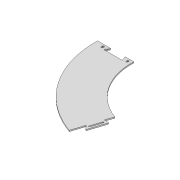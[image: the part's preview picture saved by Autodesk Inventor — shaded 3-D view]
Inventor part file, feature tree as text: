
AUTODESK INVENTOR PART (.ipt)
format: ipt  version: 2020 (Build 240168000, 168)  size: 261,120 bytes
history: native  units: mm
features: extrude x1, sketch x1
ambient origin geometry x8: Origin, YZ Plane, XZ Plane, XY Plane, X Axis, Y Axis, Z Axis, Center Point
bodies: Solid1 (feature_tree)
feature tree (2):
  extrude  "Extrusion1"  Depth=1.75mm
  sketch  "Sketch1"  dims[d0=504.787567mm d1=944.787567mm d34=1152.87mm d45=7.5mm d48=712.87mm d52=7.0mm d53=0.0mm d58=50.0mm d60=360.0deg d62=13.601997mm d63=25.0mm d65=50.0mm d71=50.0mm d72=7.5mm d74=3.5mm d75=3.5mm d79=0.0mm d80=8.0mm d81=1.75mm d83=50.0mm d84=8.0mm d85=1.75mm d86=50.0mm d88=360.0deg]
